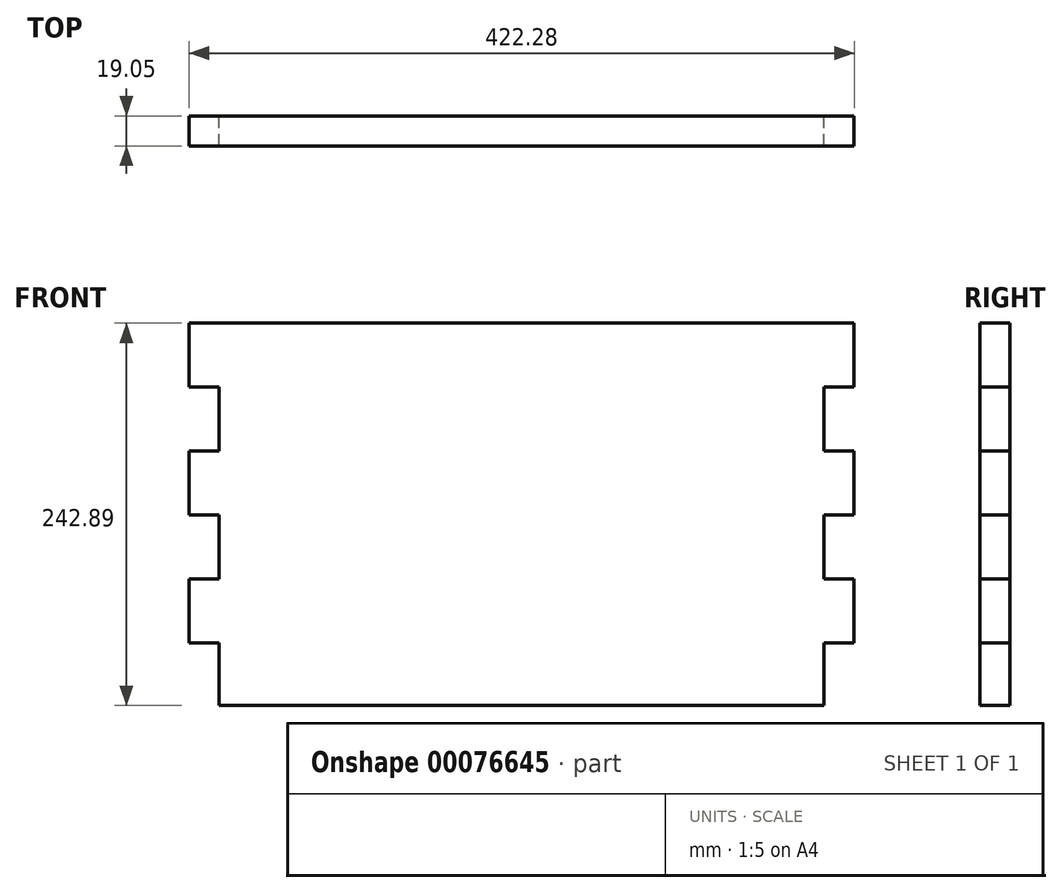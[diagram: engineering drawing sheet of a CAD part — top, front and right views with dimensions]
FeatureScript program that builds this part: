
annotation { "Feature Type Name" : "Feature", "Feature Type Description" : "" }
export const myFeature = defineFeature(function(context is Context, id is Id, definition is map)
    precondition{}
    {
        {
            var Q0;
            Q0=qCreatedBy(makeId("Front.planeOp"),FACE);
            var sketch = newSketch(context, id + "F0", { "sketchPlane" : qUnion([Q0])});
            skLineSegment(sketch, "E0.top", {"start": v(-193.16, 63.84) * mm, "end": v(-174.1, 63.84) * mm});
            skLineSegment(sketch, "E0.left", {"start": v(-193.16, 104.48) * mm, "end": v(-193.16, 63.84) * mm});
            skLineSegment(sketch, "E1.0.1.0", {"start": v(-193.16, 23.2) * mm, "end": v(-174.1, 23.2) * mm});
            skLineSegment(sketch, "E1.0.1.1", {"start": v(-174.1, 63.84) * mm, "end": v(-174.1, 23.2) * mm});
            skLineSegment(sketch, "E1.0.2.0", {"start": v(-193.16, -17.44) * mm, "end": v(-174.1, -17.44) * mm});
            skLineSegment(sketch, "E1.0.2.2", {"start": v(-193.16, 23.2) * mm, "end": v(-193.16, -17.44) * mm});
            skLineSegment(sketch, "E1.0.2.3", {"start": v(-193.16, 23.2) * mm, "end": v(-174.1, 23.2) * mm});
            skLineSegment(sketch, "E1.0.3.0", {"start": v(-193.16, -58.08) * mm, "end": v(-174.1, -58.08) * mm});
            skLineSegment(sketch, "E1.0.3.1", {"start": v(-174.1, -17.44) * mm, "end": v(-174.1, -58.08) * mm});
            skLineSegment(sketch, "E1.0.3.3", {"start": v(-193.16, -17.44) * mm, "end": v(-174.1, -17.44) * mm});
            skLineSegment(sketch, "E1.0.4.0", {"start": v(-193.16, -98.72) * mm, "end": v(-174.1, -98.72) * mm});
            skLineSegment(sketch, "E1.0.4.2", {"start": v(-193.16, -58.08) * mm, "end": v(-193.16, -98.72) * mm});
            skLineSegment(sketch, "E1.0.4.3", {"start": v(-193.16, -58.08) * mm, "end": v(-174.1, -58.08) * mm});
            skLineSegment(sketch, "E1.0.5.3", {"start": v(-193.16, -98.72) * mm, "end": v(-174.1, -98.72) * mm});
            skLineSegment(sketch, "E2", {"start": v(-174.1, -98.72) * mm, "end": v(-174.1, -138.4) * mm});
            skLineSegment(sketch, "E3", {"start": v(-193.16, 104.48) * mm, "end": v(17.98, 104.48) * mm});
            skLineSegment(sketch, "E4", {"start": v(-174.1, -138.4) * mm, "end": v(17.98, -138.4) * mm});
            skLineSegment(sketch, "E5.MirrorCS", {"start": v(229.12, 63.84) * mm, "end": v(210.07, 63.84) * mm});
            skLineSegment(sketch, "E6.MirrorCS", {"start": v(229.12, -58.08) * mm, "end": v(210.07, -58.08) * mm});
            skLineSegment(sketch, "E7.MirrorCS", {"start": v(229.12, 23.2) * mm, "end": v(210.07, 23.2) * mm});
            skLineSegment(sketch, "E8.MirrorCS", {"start": v(229.12, -98.72) * mm, "end": v(210.07, -98.72) * mm});
            skLineSegment(sketch, "E9.MirrorCS", {"start": v(229.12, -17.44) * mm, "end": v(210.07, -17.44) * mm});
            skLineSegment(sketch, "E10.MirrorCS", {"start": v(210.07, -98.72) * mm, "end": v(210.07, -138.4) * mm});
            skLineSegment(sketch, "E11.MirrorCS", {"start": v(229.12, -58.08) * mm, "end": v(229.12, -98.72) * mm});
            skLineSegment(sketch, "E12.MirrorCS", {"start": v(229.12, 104.48) * mm, "end": v(229.12, 63.84) * mm});
            skLineSegment(sketch, "E13.MirrorCS", {"start": v(229.12, 23.2) * mm, "end": v(229.12, -17.44) * mm});
            skLineSegment(sketch, "E14.MirrorCS", {"start": v(210.07, -17.44) * mm, "end": v(210.07, -58.08) * mm});
            skLineSegment(sketch, "E15.MirrorCS", {"start": v(210.07, 63.84) * mm, "end": v(210.07, 23.2) * mm});
            skLineSegment(sketch, "E16.MirrorCS", {"start": v(210.07, -138.4) * mm, "end": v(17.98, -138.4) * mm});
            skLineSegment(sketch, "E17.MirrorCS", {"start": v(229.12, 104.48) * mm, "end": v(17.98, 104.48) * mm});
            skSolve(sketch);
        }
        {
            var Q0;
            Q0 = qSketchRegion(id + "F0", true);
            extrude(context, id + "F1", {"entities" : qUnion([Q0]), "depth" : 19.05 * mm});
        }
    });
